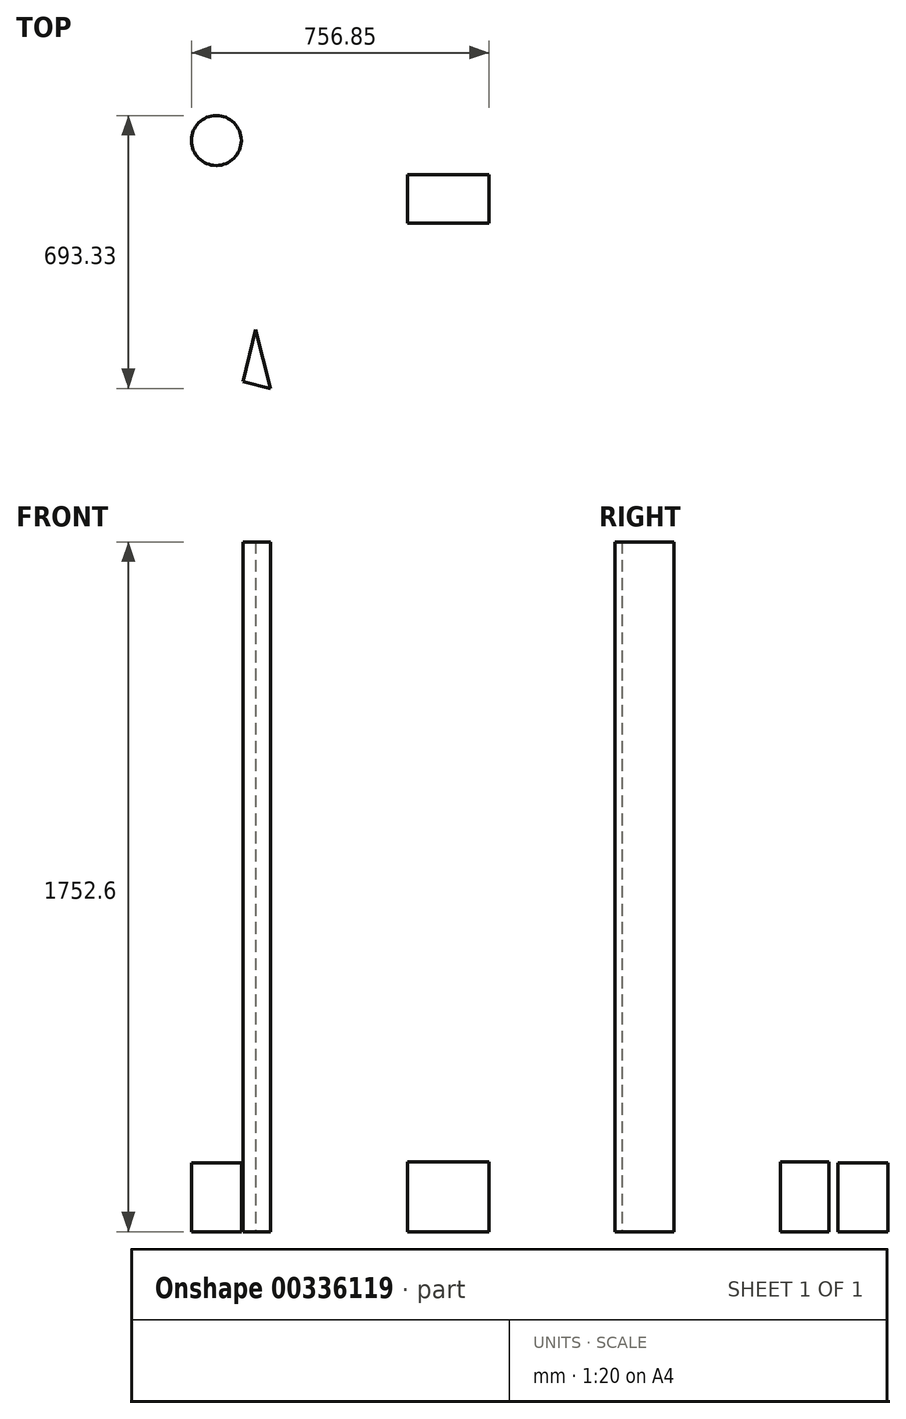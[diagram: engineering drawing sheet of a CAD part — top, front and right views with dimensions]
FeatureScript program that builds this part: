
annotation { "Feature Type Name" : "Feature", "Feature Type Description" : "" }
export const myFeature = defineFeature(function(context is Context, id is Id, definition is map)
    precondition{}
    {
        {
            var Q0;
            Q0=qCreatedBy(makeId("Top.planeOp"),FACE);
            var sketch = newSketch(context, id + "F0", { "sketchPlane" : qUnion([Q0])});
            skCircle(sketch, "E0", {"center": v(-377.32, 319.9) * mm, "radius": 63.5 * mm});
            skLineSegment(sketch, "E1.bottom", {"start": v(108.5, 232.64) * mm, "end": v(316.03, 232.64) * mm});
            skLineSegment(sketch, "E1.top", {"start": v(108.5, 110) * mm, "end": v(316.03, 110) * mm});
            skLineSegment(sketch, "E1.left", {"start": v(108.5, 232.64) * mm, "end": v(108.5, 110) * mm});
            skLineSegment(sketch, "E1.right", {"start": v(316.03, 232.64) * mm, "end": v(316.03, 110) * mm});
            skLineSegment(sketch, "E2", {"start": v(-335.96, -77.57) * mm, "end": v(-142.58, -143.6) * mm});
            skLineSegment(sketch, "E3", {"start": v(-142.58, -143.6) * mm, "end": v(-142.58, -336.98) * mm});
            skLineSegment(sketch, "E4", {"start": v(-142.58, -336.98) * mm, "end": v(-364.26, -372.36) * mm});
            skLineSegment(sketch, "E5", {"start": v(-364.26, -372.36) * mm, "end": v(-335.96, -77.57) * mm});
            skLineSegment(sketch, "E6", {"start": v(-277, -160.1) * mm, "end": v(-310.02, -292.17) * mm});
            skLineSegment(sketch, "E7", {"start": v(-310.02, -292.17) * mm, "end": v(-239, -309.93) * mm});
            skLineSegment(sketch, "E8", {"start": v(-239, -309.93) * mm, "end": v(-277, -160.1) * mm});
            skSolve(sketch);
        }
        {
            var Q0;
            Q0=makeQuery(id+"F0.imprint","IMPRINT",FACE,{"disambiguationData":[TD([[makeQuery(id+"F0.imprint","IMPRINT",EDGE,{"derivedFrom":sQuery(id+"F0.wireOp",EDGE,"E0")}),1.0]])]});
            extrude(context, id + "F1", {"entities" : qUnion([Q0]), "depth" : 175.26 * mm});
        }
        {
            var Q0;
            Q0=makeQuery(id+"F0.imprint","IMPRINT",FACE,{"disambiguationData":[TD([[makeQuery(id+"F0.imprint","IMPRINT",EDGE,{"derivedFrom":sQuery(id+"F0.wireOp",EDGE,"E1.bottom")}),-1.0]])]});
            extrude(context, id + "F2", {"entities" : qUnion([Q0]), "depth" : 177.8 * mm});
        }
        {
            var Q0;
            Q0=makeQuery(id+"F0.imprint","IMPRINT",FACE,{"disambiguationData":[TD([[makeQuery(id+"F0.imprint","IMPRINT",EDGE,{"derivedFrom":sQuery(id+"F0.wireOp",EDGE,"E6")}),1.0]])]});
            extrude(context, id + "F3", {"entities" : qUnion([Q0]), "depth" : 1752.6 * mm});
        }
    });
